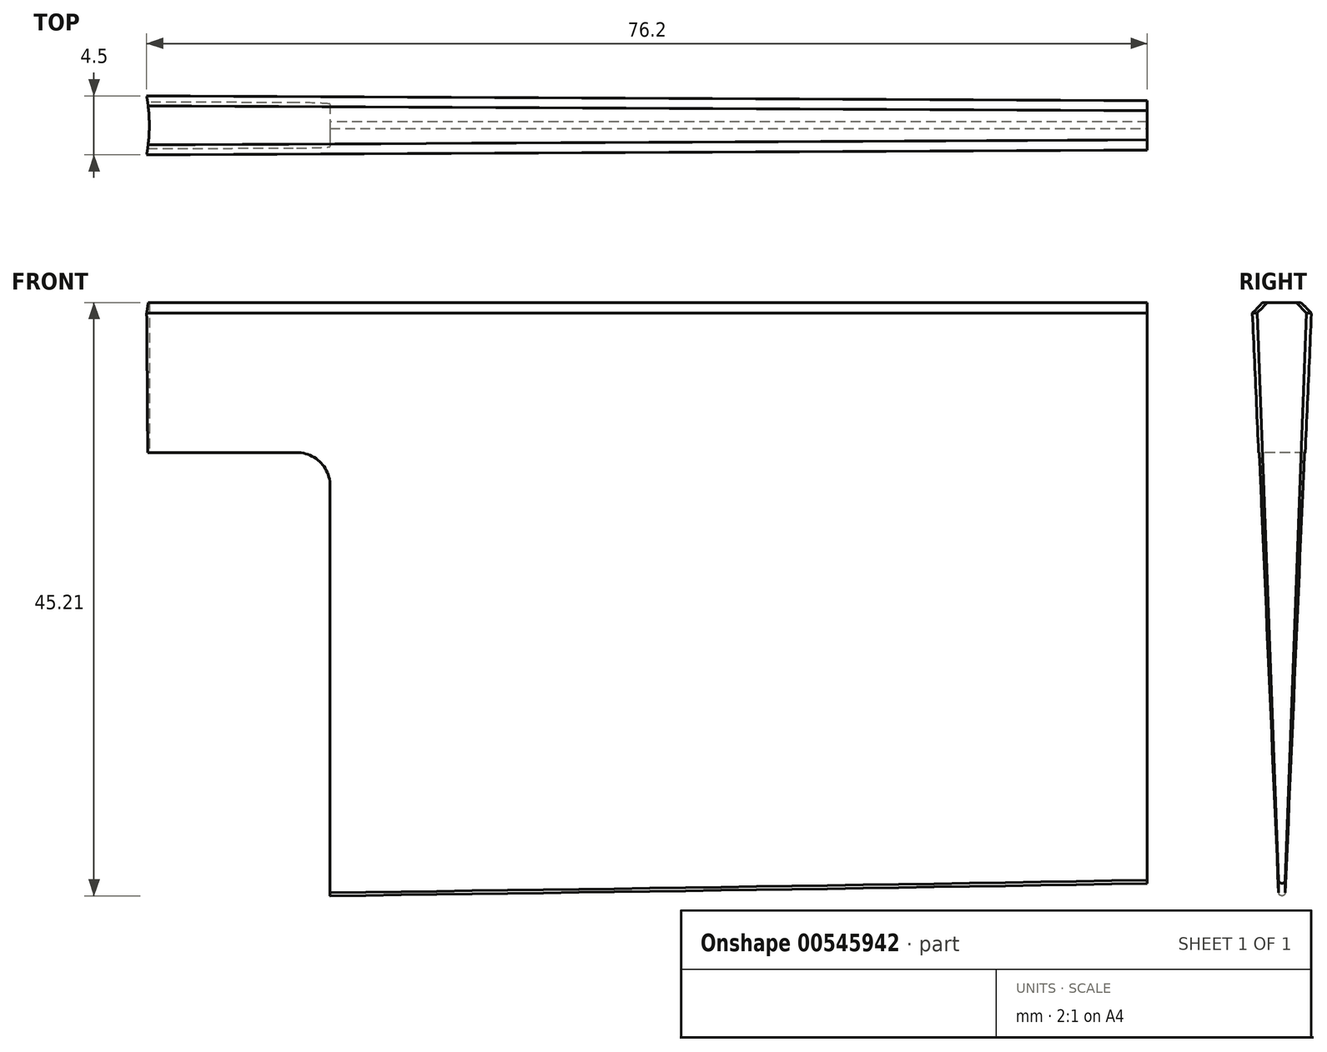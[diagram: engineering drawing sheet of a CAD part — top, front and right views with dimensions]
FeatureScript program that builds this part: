
annotation { "Feature Type Name" : "Feature", "Feature Type Description" : "" }
export const myFeature = defineFeature(function(context is Context, id is Id, definition is map)
    precondition{}
    {
        {
            var Q0;
            Q0=qCreatedBy(makeId("Right.planeOp"),FACE);
            var sketch = newSketch(context, id + "F0", { "sketchPlane" : qUnion([Q0])});
            skLineSegment(sketch, "E0", {"start": v(0, 0) * mm, "end": v(2.29, 50.75) * mm});
            skLineSegment(sketch, "E1", {"start": v(-2.29, 50.76) * mm, "end": v(0, 0) * mm});
            skLineSegment(sketch, "E2", {"start": v(-2.29, 50.76) * mm, "end": v(2.29, 50.75) * mm});
            skSolve(sketch);
        }
        {
            var Q0;
            Q0=qCreatedBy(makeId("Right.planeOp"),FACE);
            cPlane(context, id + "F1", {"entities" : qUnion([Q0]), "cplaneType" : CPlaneType.OFFSET, "offset" : 76.2 * mm, "width" : 152.4 * mm, "height" : 152.4 * mm});
        }
        {
            var Q0;
            Q0=qCreatedBy(id+"F1.planeOp",FACE);
            var sketch = newSketch(context, id + "F2", { "sketchPlane" : qUnion([Q0])});
            skLineSegment(sketch, "E3", {"start": v(0, 0) * mm, "end": v(1.9, 50.76) * mm});
            skLineSegment(sketch, "E4", {"start": v(-1.9, 50.78) * mm, "end": v(0, 0) * mm});
            skLineSegment(sketch, "E5", {"start": v(-1.9, 50.78) * mm, "end": v(1.9, 50.76) * mm});
            skSolve(sketch);
        }
        {
            var Q0;
            Q0=makeQuery(id+"F0.imprint","IMPRINT",FACE,{"disambiguationData":[TD([[makeQuery(id+"F0.imprint","IMPRINT",EDGE,{"derivedFrom":sQuery(id+"F0.wireOp",EDGE,"E0")}),1.0]])]});
            var Q1;
            Q1=makeQuery(id+"F2.imprint","IMPRINT",FACE,{"disambiguationData":[TD([[makeQuery(id+"F2.imprint","IMPRINT",EDGE,{"derivedFrom":sQuery(id+"F2.wireOp",EDGE,"E3")}),1.0]])]});
            loft(context, id + "F3", {"sheetProfilesArray" : [{ "sheetProfileEntities" : qUnion([Q0]) }, { "sheetProfileEntities" : qUnion([Q1]) }]});
        }
        {
            var Q0;
            Q0=qCreatedBy(makeId("Front.planeOp"),FACE);
            var sketch = newSketch(context, id + "F4", { "sketchPlane" : qUnion([Q0])});
            skLineSegment(sketch, "E6.bottom", {"start": v(0, -7.92) * mm, "end": v(13.97, -7.92) * mm});
            skLineSegment(sketch, "E6.top", {"start": v(0, 39.35) * mm, "end": v(13.97, 39.35) * mm});
            skLineSegment(sketch, "E6.left", {"start": v(0, -7.92) * mm, "end": v(0, 39.35) * mm});
            skLineSegment(sketch, "E6.right", {"start": v(13.97, -7.92) * mm, "end": v(13.97, 39.35) * mm});
            skPoint(sketch, "E7.0", {"position": v(0, 52.05) * mm});
            skSolve(sketch);
        }
        {
            var Q0;
            Q0=qSketchRegion(id+"F4",true);
            extrude(context, id + "F5", {"entities" : qUnion([Q0]), "operationType" : NewBodyOperationType.REMOVE, "endBound" : BoundingType.SYMMETRIC, "oppositeDirection" : true, "depth" : 25.4 * mm, "offsetDistance" : 25.4 * mm});
        }
        {
            var Q0;
            Q0=makeQuery(id+"F5.boolean.opBoolean","COPY",EDGE,{"derivedFrom":makeQuery(id+"F5.opExtrude","SWEPT_EDGE",EDGE,{"disambiguationData":[OSD([sQuery(id+"F4.wireOp",EDGE,"E6.top"),sQuery(id+"F4.wireOp",EDGE,"E6.right")])]})});
            fillet(context, id + "F6", {"entities" : qUnion([Q0]), "radius" : 2.54 * mm, "tangentPropagation" : true, "allowEdgeOverflow" : false});
        }
        {
            var Q0;
            Q0=makeQuery(id+"F3.opLoft","SWEPT_EDGE",EDGE,{"disambiguationData":[OSD([sQuery(id+"F0.wireOp",EDGE,"E0"),sQuery(id+"F0.wireOp",EDGE,"E1"),sQuery(id+"F2.wireOp",EDGE,"E3"),sQuery(id+"F2.wireOp",EDGE,"E4")])]});
            fillet(context, id + "F7", {"entities" : qUnion([Q0]), "radius" : 0.25 * mm, "tangentPropagation" : true, "allowEdgeOverflow" : false});
        }
        {
            var Q0;
            Q0=makeQuery(id+"F3.opLoft","SWEPT_EDGE",EDGE,{"disambiguationData":[OSD([sQuery(id+"F0.wireOp",EDGE,"E1"),sQuery(id+"F0.wireOp",EDGE,"E2"),sQuery(id+"F2.wireOp",EDGE,"E4"),sQuery(id+"F2.wireOp",EDGE,"E5")])]});
            var Q1;
            Q1=makeQuery(id+"F3.opLoft","SWEPT_EDGE",EDGE,{"disambiguationData":[OSD([sQuery(id+"F0.wireOp",EDGE,"E0"),sQuery(id+"F0.wireOp",EDGE,"E2"),sQuery(id+"F2.wireOp",EDGE,"E3"),sQuery(id+"F2.wireOp",EDGE,"E5")])]});
            chamfer(context, id + "F8", {"entities" : qUnion([Q0, Q1]), "width" : 0.76 * mm, "tangentPropagation" : true});
        }
        {
            var Q0;
            Q0=makeQuery(id+"F5.boolean.opBoolean","COPY",FACE,{"derivedFrom":makeQuery(id+"F5.opExtrude","SWEPT_FACE",FACE,{"disambiguationData":[OSD([sQuery(id+"F4.wireOp",EDGE,"E6.top")])]})});
            var sketch = newSketch(context, id + "F9", { "sketchPlane" : qUnion([Q0])});
            skPoint(sketch, "E8.0", {"position": v(0, 2.25) * mm});
            skPoint(sketch, "E9.0", {"position": v(0, -2.25) * mm});
            skArc(sketch, "E10", {"start": v(0, -2.25) * mm, "mid": v(0.2, 0) * mm, "end": v(0, 2.25) * mm});
            skLineSegment(sketch, "E11", {"start": v(0, 2.25) * mm, "end": v(0, -2.25) * mm});
            skSolve(sketch);
        }
        {
            var Q0;
            Q0 = qSketchRegion(id + "F9", true);
            extrude(context, id + "F10", {"entities" : qUnion([Q0]), "operationType" : NewBodyOperationType.REMOVE, "endBound" : BoundingType.THROUGH_ALL, "oppositeDirection" : true, "depth" : 25.4 * mm, "offsetDistance" : 25.4 * mm});
        }
    });
